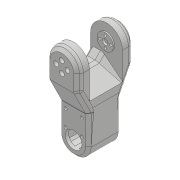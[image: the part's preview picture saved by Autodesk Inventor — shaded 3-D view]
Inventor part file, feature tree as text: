
AUTODESK INVENTOR PART (.ipt)
format: ipt  version: 2018 (Build 220112000, 112)  size: 1,055,232 bytes
history: native  units: mm
features: projected_geometry x42, sketch x40, extrude x33, fillet x13, chamfer x11, hole x8, other x4, mirror x1, reference x1
ambient origin geometry x8: Origin, YZ Plane, XZ Plane, XY Plane, X Axis, Y Axis, Z Axis, Center Point
bodies: Solid1 (feature_tree)
feature tree (153):
  extrude  "Extrusion1"  Depth=45.0mm
  extrude  "Extrusion2"  Depth=2.25mm
  hole  "Hole1"  [1 undecoded]
  hole  "Hole2"  [1 undecoded]
  fillet  "Fillet1"  Radius=14.0mm
  extrude  "Extrusion3"  Depth=18.5mm
  extrude  "Extrusion4"  Depth=10.0mm
  extrude  "Extrusion5"  Depth=2.0mm
  extrude  "Extrusion6"  Depth=2.0mm
  hole  "Hole3"  [1 undecoded]
  extrude  "Extrusion7"  Depth=0.5mm
  extrude  "Extrusion8"  Depth=5.0mm TaperAngle=0.0deg
  extrude  "Extrusion9"  Depth=10.0mm
  extrude  "Extrusion10"  Depth=10.0mm
  extrude  "Extrusion11"  Depth=14.5mm
  extrude  "Extrusion12"  Depth=20.0mm
  extrude  "Extrusion13"  Depth=5.0mm
  extrude  "Extrusion14"  Depth=5.0mm
  extrude  "Extrusion15"  Depth=5.0mm
  extrude  "Extrusion16"  Depth=5.0mm
  extrude  "Extrusion17"  Depth=1.0mm
  chamfer  "Chamfer1"  Distance=1.0mm
  fillet  "Fillet7"  Radius=20.7mm
  fillet  "Fillet8"  Radius=32.0mm
  mirror  "Mirror1"
  extrude  "Extrusion19"  Depth=1.0mm TaperAngle=0.0deg
  extrude  "Extrusion20"  Depth=8.0mm
  extrude  "Extrusion21"  Depth=0.2mm TaperAngle=0.0deg
  extrude  "Extrusion22"  Depth=0.5mm TaperAngle=0.0deg
  extrude  "Extrusion23"  Depth=9.0mm TaperAngle=0.0deg
  extrude  "Extrusion24"  Depth=2.0mm TaperAngle=0.0deg
  chamfer  "Chamfer2"  Distance=0.2mm
  chamfer  "Chamfer8"  Distance=2.0mm Angle=45.0deg
  extrude  "Extrusion25"  Depth=0.5mm
  extrude  "Extrusion26"  Depth=2.0mm TaperAngle=0.0deg
  chamfer  "Chamfer3"  Distance=2.0mm
  chamfer  "Chamfer4"  Distance=2.0mm
  chamfer  "Chamfer5"  Distance=15.0mm
  chamfer  "Chamfer6"  Distance=56.1mm
  fillet  "Fillet9"  Radius=41.6mm
  fillet  "Fillet10"  Radius=41.0mm
  hole  "Hole6"  [1 undecoded]
  fillet  "Fillet12"  Radius=7.0mm
  hole  "Hole7"  [1 undecoded]
  extrude  "Extrusion27"  Depth=3.0mm TaperAngle=45.0deg
  extrude  "Extrusion28"  Depth=5.0mm TaperAngle=45.0deg
  hole  "Hole8"  [1 undecoded]
  extrude  "Extrusion29"  Depth=2.0mm
  chamfer  "Chamfer7"  Distance=1.0mm
  fillet  "Fillet13"  Radius=20.5mm
  extrude  "Extrusion30"  Depth=1.0mm TaperAngle=0.0deg
  extrude  "Extrusion31"  Depth=1.0mm
  fillet  "Fillet14"  Radius=3.1mm
  extrude  "Extrusion32"  Depth=14.0mm
  fillet  "Fillet15"  Radius=16.0mm
  fillet  "Fillet18"  Radius=3.1mm
  extrude  "Extrusion35"  Depth=2.0mm TaperAngle=45.0deg
  extrude  "Extrusion36"  Depth=1.0mm
  chamfer  "Chamfer9"  Distance=37.0mm
  chamfer  "Chamfer10"  Distance=10.0mm
  chamfer  "Chamfer11"  Distance=7.5mm
  fillet  "Fillet19"  Radius=6.0mm
  hole  "Hole9"  [1 undecoded]
  fillet  "Fillet20"  Radius=6.0mm
  hole  "Hole10"  [1 undecoded]
  fillet  "Fillet21"  Radius=5.0mm
  sketch  "Sketch1"  dims[d0=24.5mm d1=45.0mm]
  sketch  "Sketch2"  dims[d2=1.95mm d3=0.0mm d4=2.25mm]
  projected_geometry  "Projected Loop1"
  sketch  "Sketch3"  dims[d5=20.0mm d6=2.25mm]
  projected_geometry  "Projected Loop2"
  sketch  "Sketch4"  dims[d7=5.25mm d8=5.25mm d9=14.0mm]
  projected_geometry  "Projected Loop3"
  sketch  "Sketch5"  dims[d10=5.25mm d11=18.5mm]
  projected_geometry  "Projected Loop4"
  sketch  "Sketch6"  dims[d12=10.0mm d13=0.0mm d14=20.5mm]
  projected_geometry  "Projected Loop5"
  sketch  "Sketch7"  dims[d15=2.0mm d16=2.195mm]
  projected_geometry  "Projected Loop6"
  sketch  "Sketch8"  dims[d17=2.0mm]
  projected_geometry  "Projected Loop7"
  sketch  "Sketch9"  dims[d18=2.4mm d19=6.0mm d20=4.4mm d21=2.0mm d22=90.0deg d23=8.0mm d24=20.594885mm d25=20.5mm]
  projected_geometry  "Projected Loop8"
  projected_geometry  "Projected Loop9"
  sketch  "Sketch10"  dims[d26=26.65mm d27=2.0mm]
  projected_geometry  "Projected Loop10"
  projected_geometry  "Projected Loop11"
  sketch  "Sketch11"  dims[d28=2.0mm]
  projected_geometry  "Projected Loop12"
  sketch  "Sketch12"  dims[d29=2.4mm d30=6.0mm d31=4.4mm d32=2.0mm d33=90.0deg d34=8.0mm d35=20.594885mm d36=0.5mm]
  sketch  "Sketch13"  dims[d37=18.0mm d38=5.0mm d39=0.0mm]
  sketch  "Sketch14"  dims[d41=10.0mm d42=0.0mm d43=24.5mm]
  projected_geometry  "Projected Loop13"
  sketch  "Sketch15"  dims[d44=1.15mm d45=0.0mm d46=10.0mm]
  sketch  "Sketch16"  dims[d47=21.0mm d48=14.5mm]
  projected_geometry  "Projected Loop14"
  sketch  "Sketch17"  dims[d49=20.0mm d50=14.5mm]
  projected_geometry  "Projected Loop15"
  sketch  "Sketch18"  dims[d51=24.5mm d52=5.0mm]
  projected_geometry  "Projected Loop16"
  sketch  "Sketch19"  dims[d53=5.0mm d54=2.25mm]
  projected_geometry  "Projected Loop17"
  sketch  "Sketch20"  dims[d55=2.25mm d56=5.0mm]
  projected_geometry  "Projected Loop18"
  sketch  "Sketch25"  dims[d57=5.0mm d58=9.0mm]
  projected_geometry  "Projected Loop22"
  sketch  "Sketch26"  dims[d59=14.75mm d60=4.0mm d61=1.0mm d62=0.0mm d63=20.7mm]
  projected_geometry  "Projected Loop23"
  sketch  "Sketch27"  dims[d64=2.4mm d65=6.0mm d66=4.4mm d67=2.0mm d68=90.0deg d69=8.0mm d70=20.594885mm d72=32.0mm]
  projected_geometry  "Projected Loop24"
  sketch  "Sketch28"  dims[d73=5.0mm d74=0.0mm d75=1.0mm d76=0.0mm]
  projected_geometry  "Projected Loop25"
  sketch  "Sketch29"  dims[d77=12.25mm d78=0.0mm d80=8.0mm]
  projected_geometry  "Projected Loop26"
  sketch  "Sketch30"  dims[d81=4.5mm d82=0.0mm d84=0.2mm d85=0.0mm]
  projected_geometry  "Projected Loop27"
  sketch  "Sketch31"  dims[d86=21.0mm d87=0.5mm d88=0.0mm]
  sketch  "Sketch33"  dims[d91=8.0mm d92=0.0mm d93=9.0mm d94=0.0mm]
  projected_geometry  "Projected Loop28"
  projected_geometry  "Projected Loop29"
  projected_geometry  "Projected Loop30"
  sketch  "Sketch34"  dims[d95=5.0mm d96=0.0mm d98=0.2mm d99=0.0mm d100=0.2mm d101=0.0mm d102=2.5mm d103=2.0mm d104=45.0deg]
  projected_geometry  "Projected Loop31"
  projected_geometry  "Projected Loop32"
  sketch  "Sketch35"  dims[d105=1.5mm d114=0.5mm]
  projected_geometry  "Projected Loop33"
  sketch  "Sketch36"  dims[d128=2.0mm d129=0.0mm d130=2.0mm d131=0.0mm]
  projected_geometry  "Projected Loop34"
  sketch  "Sketch37"  dims[d132=40.0mm d133=2.0mm d134=0.0mm d135=2.0mm d136=0.0mm]
  projected_geometry  "Projected Loop35"
  sketch  "Sketch38"  dims[d137=40.0mm]
  projected_geometry  "Projected Loop36"
  sketch  "Sketch39"  dims[d138=70.0mm d139=15.0mm d140=0.0mm d141=56.1mm d142=0.0mm]
  projected_geometry  "Projected Loop37"
  sketch  "Sketch40"  dims[d143=4.0mm d144=8.0mm d145=45.0deg d146=41.6mm d147=41.0mm]
  projected_geometry  "Projected Loop38"
  sketch  "Sketch41"  dims[d148=7.0mm d149=7.0mm d150=7.0mm]
  projected_geometry  "Projected Loop39"
  reference  "Reference1"
  sketch  "Sketch44"  dims[d151=100.0mm d152=0.0mm d153=15.282752mm]
  projected_geometry  "Projected Loop42"
  sketch  "Sketch45"  dims[d156=100.0mm d157=0.0mm d158=3.0mm d159=2.0mm d160=45.0deg]
  projected_geometry  "Projected Loop43"
  sketch  "Sketch46"  dims[d161=5.0mm d162=2.0mm d163=45.0deg d164=5.0mm d165=2.0mm d166=45.0deg]
  projected_geometry  "Projected Loop44"
  sketch  "Sketch47"  dims[d167=5.0mm d168=2.0mm d169=45.0deg d170=5.0mm d171=2.0mm d173=5.7mm d174=6.0mm d175=4.0mm d176=2.0mm d177=90.0deg d178=25.0mm d179=0.0mm d180=1.0mm d181=2.459mm d182=25.0mm d183=4.0mm d184=2.0mm d185=90.0deg d186=25.0mm d187=20.594885mm d188=20.5mm d189=1.6mm d190=0.0mm d191=20.5mm d192=3.1mm d193=0.0mm d194=14.0mm d195=3.2mm d196=25.0mm d197=6.3mm d198=2.0mm d199=90.0deg d200=25.0mm d201=20.594885mm d202=16.0mm d203=3.1mm d204=0.0mm d205=1.5mm d206=2.0mm d207=45.0deg d208=1.7mm d209=37.0mm d210=10.0mm d211=0.0mm d212=7.5mm d213=6.0mm d214=6.0mm d215=6.0mm d216=6.0mm d217=5.0mm d218=0.0mm d219=1.5mm d220=6.0mm d221=6.0mm d222=6.0mm d223=6.0mm d224=6.0mm d225=0.0mm d226=1.5mm d231=4.0mm d232=8.0mm d233=45.0deg d234=10.0mm d237=7.0mm d238=2.5mm d239=0.0mm d240=7.0mm d241=2.5mm d242=0.0mm d243=14.0mm d244=25.0mm d245=45.0deg d246=14.0mm d247=25.0mm d248=45.0deg d249=14.0mm d250=25.0mm d251=45.0deg d252=10.0mm d253=4.0mm d254=6.0mm d255=4.0mm d256=2.0mm d257=90.0deg d258=2.0mm d259=20.594885mm d260=1.0mm d261=4.0mm d262=6.0mm d263=4.0mm d264=2.0mm d265=90.0deg d266=2.0mm d267=20.594885mm d268=1.0mm]
  projected_geometry  "Projected Loop45"
  projected_geometry  "Project Cut Edges1"
  projected_geometry  "Project Cut Edges2"
  parser-record x1  (decoder bookkeeping rows leaked as tree rows — omitted from the tree; the rows remain in map.json)
  other  "servocheck.iam"
  other  "bottomarm:1"
  other  "arm1:1"
note: 8 required parameter values undecoded (feature->parameter linkage not recoverable at this tier; creation-order binding heuristic only, values carry confidence <= 0.55)
note: 1 file-system path scrubbed to <path> (originals preserved in map.json)
